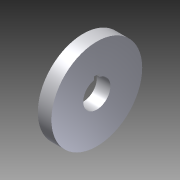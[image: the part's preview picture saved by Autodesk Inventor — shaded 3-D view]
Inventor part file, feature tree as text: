
AUTODESK INVENTOR PART (.ipt)
format: ipt  version: 2012 (Build 160160000, 160)  size: 643,584 bytes
history: native  units: in
note: dims shown in document units (in); Inventor stores cm internally (conversion verified against a paired STEP export)
features: extrude x4, sketch x1, imported_body x1
ambient origin geometry x8: Origin, YZ Plane, XZ Plane, XY Plane, X Axis, Y Axis, Z Axis, Center Point
feature tree (6):
  sketch  "Sketch1"  dims[d0=0.375in d3=0.3in d4=0.0in d5=1.0in d6=0.0787in d7=0.0787in d8=0.0394in d9=0.2269in d10=0.375in d11=0.0in d12=1.25in d13=1.0in d14=0.0in d15=1.0in d16=0.0in]
  extrude  "Extrusion2"  Depth=0.3in TaperAngle=0.0deg
  extrude  "Extrusion3"  Depth=1.0in
  extrude  "Extrusion4"  Depth=0.0787in
  extrude  "Extrusion5"  Depth=0.0787in
  imported_body  "Base1"
